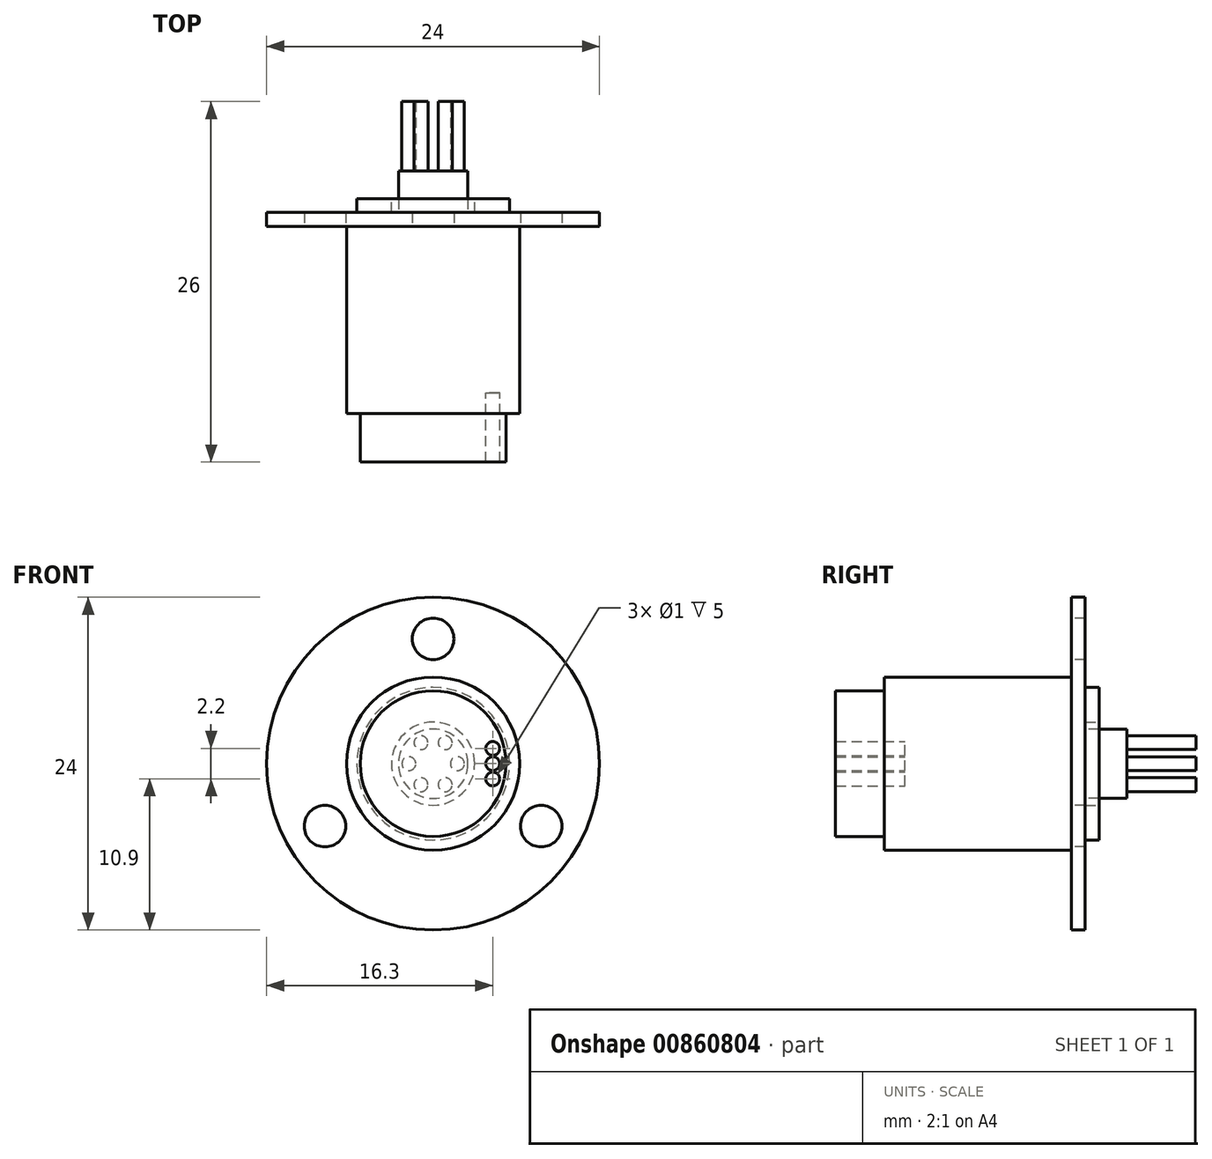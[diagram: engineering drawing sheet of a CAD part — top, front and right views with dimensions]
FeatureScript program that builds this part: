
annotation { "Feature Type Name" : "Feature", "Feature Type Description" : "" }
export const myFeature = defineFeature(function(context is Context, id is Id, definition is map)
    precondition{}
    {
        {
            var Q0;
            Q0=qCreatedBy(makeId("Front.planeOp"),FACE);
            var sketch = newSketch(context, id + "F0", { "sketchPlane" : qUnion([Q0])});
            skCircle(sketch, "E0", {"center": v(0, 0) * mm, "radius": 6.25 * mm});
            skSolve(sketch);
        }
        {
            var Q0;
            Q0=makeQuery(id+"F0.imprint","IMPRINT",FACE,{"disambiguationData":[TD([[makeQuery(id+"F0.imprint","IMPRINT",EDGE,{"derivedFrom":sQuery(id+"F0.wireOp",EDGE,"E0")}),1.0]])]});
            extrude(context, id + "F1", {"entities" : qUnion([Q0]), "depth" : 13.5 * mm, "offsetDistance" : 25 * mm});
        }
        {
            var Q0;
            Q0=makeQuery(id+"F1.opExtrude","CAP_FACE",FACE,{"disambiguationData":[OSD([sQuery(id+"F0.wireOp",EDGE,"E0")])],"isStart":true});
            var sketch = newSketch(context, id + "F2", { "sketchPlane" : qUnion([Q0])});
            skCircle(sketch, "E1", {"center": v(0, 0) * mm, "radius": 12 * mm});
            skCircle(sketch, "E2", {"center": v(0, 9) * mm, "radius": 1.5 * mm});
            skCircle(sketch, "E3.1.0", {"center": v(-7.8, -4.5) * mm, "radius": 1.5 * mm});
            skCircle(sketch, "E3.2.0", {"center": v(7.8, -4.5) * mm, "radius": 1.5 * mm});
            skSolve(sketch);
        }
        {
            var Q0;
            Q0=makeQuery(id+"F2.imprint","IMPRINT",FACE,{"disambiguationData":[TD([[makeQuery(id+"F2.imprint","IMPRINT",EDGE,{"derivedFrom":sQuery(id+"F2.wireOp",EDGE,"E1")}),1.0]])]});
            var Q1;
            Q1=makeQuery(id+"F2.imprint","IMPRINT",FACE,{"disambiguationData":[TD([[makeQuery(id+"F2.imprint","IMPRINT",EDGE,{"derivedFrom":makeQuery(id+"F1.opExtrude","CAP_EDGE",EDGE,{"disambiguationData":[OSD([sQuery(id+"F0.wireOp",EDGE,"E0")])],"isStart":true})}),-1.0]])]});
            extrude(context, id + "F3", {"entities" : qUnion([Q0, Q1]), "operationType" : NewBodyOperationType.ADD, "depth" : 1 * mm, "offsetDistance" : 25 * mm});
        }
        {
            var Q0;
            Q0=makeQuery(id+"F3.opExtrude","CAP_FACE",FACE,{"disambiguationData":[OSD([sQuery(id+"F2.wireOp",EDGE,"E1"),sQuery(id+"F2.wireOp",EDGE,"E2"),sQuery(id+"F2.wireOp",EDGE,"E3.1.0"),sQuery(id+"F2.wireOp",EDGE,"E3.2.0")])],"isStart":false});
            var sketch = newSketch(context, id + "F4", { "sketchPlane" : qUnion([Q0])});
            skCircle(sketch, "E4", {"center": v(0, 0) * mm, "radius": 2.5 * mm});
            skCircle(sketch, "E5", {"center": v(0, 0) * mm, "radius": 5.5 * mm});
            skSolve(sketch);
        }
        {
            var Q0;
            Q0=makeQuery(id+"F4.imprint","IMPRINT",FACE,{"disambiguationData":[TD([[makeQuery(id+"F4.imprint","IMPRINT",EDGE,{"derivedFrom":sQuery(id+"F4.wireOp",EDGE,"E4")}),-1.0]])]});
            extrude(context, id + "F5", {"entities" : qUnion([Q0]), "operationType" : NewBodyOperationType.ADD, "depth" : 1 * mm, "offsetDistance" : 25 * mm});
        }
        {
            var Q0;
            Q0=makeQuery(id+"F5.boolean.opBoolean","SPLIT",FACE,{"disambiguationData":[TD([makeQuery(id+"F5.opExtrude","SWEPT_FACE",FACE,{"disambiguationData":[OSD([sQuery(id+"F4.wireOp",EDGE,"E4")])]})])],"derivedFrom":makeQuery(id+"F3.opExtrude","CAP_FACE",FACE,{"disambiguationData":[OSD([sQuery(id+"F2.wireOp",EDGE,"E1"),sQuery(id+"F2.wireOp",EDGE,"E2"),sQuery(id+"F2.wireOp",EDGE,"E3.1.0"),sQuery(id+"F2.wireOp",EDGE,"E3.2.0")])],"isStart":false})});
            extrude(context, id + "F6", {"entities" : qUnion([Q0]), "operationType" : NewBodyOperationType.ADD, "depth" : 3 * mm, "offsetDistance" : 25 * mm});
        }
        {
            var Q0;
            Q0=makeQuery(id+"F5.opExtrude","CAP_FACE",FACE,{"disambiguationData":[OSD([sQuery(id+"F4.wireOp",EDGE,"E4"),sQuery(id+"F4.wireOp",EDGE,"E5")])],"isStart":false});
            var sketch = newSketch(context, id + "F7", { "sketchPlane" : qUnion([Q0])});
            skCircle(sketch, "E6", {"center": v(0, 0) * mm, "radius": 3 * mm});
            skSolve(sketch);
        }
        {
            var Q0;
            Q0=makeQuery(id+"F7.imprint","IMPRINT",FACE,{"disambiguationData":[TD([[makeQuery(id+"F7.imprint","IMPRINT",EDGE,{"derivedFrom":sQuery(id+"F7.wireOp",EDGE,"E6")}),1.0]])]});
            extrude(context, id + "F8", {"entities" : qUnion([Q0]), "operationType" : NewBodyOperationType.REMOVE, "oppositeDirection" : true, "depth" : 1 * mm, "offsetDistance" : 25 * mm});
        }
        {
            var Q0;
            Q0=makeQuery(id+"F1.opExtrude","CAP_FACE",FACE,{"disambiguationData":[OSD([sQuery(id+"F0.wireOp",EDGE,"E0")])],"isStart":false});
            var sketch = newSketch(context, id + "F9", { "sketchPlane" : qUnion([Q0])});
            skCircle(sketch, "E7", {"center": v(0, 0) * mm, "radius": 5.25 * mm});
            skSolve(sketch);
        }
        {
            var Q0;
            Q0=makeQuery(id+"F9.imprint","IMPRINT",FACE,{"disambiguationData":[TD([[makeQuery(id+"F9.imprint","IMPRINT",EDGE,{"derivedFrom":sQuery(id+"F9.wireOp",EDGE,"E7")}),1.0]])]});
            extrude(context, id + "F10", {"entities" : qUnion([Q0]), "operationType" : NewBodyOperationType.REMOVE, "oppositeDirection" : true, "depth" : 1.5 * mm, "offsetDistance" : 25 * mm});
        }
        {
            var Q0;
            Q0=makeQuery(id+"F10.boolean.opBoolean","COPY",FACE,{"derivedFrom":makeQuery(id+"F10.opExtrude","CAP_FACE",FACE,{"disambiguationData":[OSD([sQuery(id+"F9.wireOp",EDGE,"E7")])],"isStart":false})});
            var sketch = newSketch(context, id + "F11", { "sketchPlane" : qUnion([Q0])});
            skCircle(sketch, "E8", {"center": v(-4.3, 0) * mm, "radius": 0.5 * mm});
            skCircle(sketch, "E9", {"center": v(-4.3, -1.1) * mm, "radius": 0.5 * mm});
            skCircle(sketch, "E10", {"center": v(-4.3, 1.1) * mm, "radius": 0.5 * mm});
            skCircle(sketch, "E11.MirrorC", {"center": v(4.3, 1.1) * mm, "radius": 0.5 * mm});
            skCircle(sketch, "E12.MirrorC", {"center": v(4.3, 0) * mm, "radius": 0.5 * mm});
            skCircle(sketch, "E13.MirrorC", {"center": v(4.3, -1.1) * mm, "radius": 0.5 * mm});
            skSolve(sketch);
        }
        {
            var Q0;
            Q0=makeQuery(id+"F11.imprint","IMPRINT",FACE,{"disambiguationData":[TD([[makeQuery(id+"F11.imprint","IMPRINT",EDGE,{"derivedFrom":sQuery(id+"F11.wireOp",EDGE,"E9")}),1.0]])]});
            var Q1;
            Q1=makeQuery(id+"F11.imprint","IMPRINT",FACE,{"disambiguationData":[TD([[makeQuery(id+"F11.imprint","IMPRINT",EDGE,{"derivedFrom":sQuery(id+"F11.wireOp",EDGE,"E8")}),1.0]])]});
            var Q2;
            Q2=makeQuery(id+"F11.imprint","IMPRINT",FACE,{"disambiguationData":[TD([[makeQuery(id+"F11.imprint","IMPRINT",EDGE,{"derivedFrom":sQuery(id+"F11.wireOp",EDGE,"E10")}),1.0]])]});
            var Q3;
            Q3=makeQuery(id+"F11.imprint","IMPRINT",FACE,{"disambiguationData":[TD([[makeQuery(id+"F11.imprint","IMPRINT",EDGE,{"derivedFrom":sQuery(id+"F11.wireOp",EDGE,"E11.MirrorC")}),-1.0]])]});
            var Q4;
            Q4=makeQuery(id+"F11.imprint","IMPRINT",FACE,{"disambiguationData":[TD([[makeQuery(id+"F11.imprint","IMPRINT",EDGE,{"derivedFrom":sQuery(id+"F11.wireOp",EDGE,"E12.MirrorC")}),-1.0]])]});
            var Q5;
            Q5=makeQuery(id+"F11.imprint","IMPRINT",FACE,{"disambiguationData":[TD([[makeQuery(id+"F11.imprint","IMPRINT",EDGE,{"derivedFrom":sQuery(id+"F11.wireOp",EDGE,"E13.MirrorC")}),-1.0]])]});
            extrude(context, id + "F12", {"entities" : qUnion([Q0, Q1, Q2, Q3, Q4, Q5]), "operationType" : NewBodyOperationType.ADD, "depth" : 5 * mm, "offsetDistance" : 25 * mm});
        }
        {
            var Q0;
            Q0=makeQuery(id+"F6.opExtrude","CAP_FACE",FACE,{"disambiguationData":[OSD([sQuery(id+"F2.wireOp",EDGE,"E1"),sQuery(id+"F2.wireOp",EDGE,"E2"),sQuery(id+"F2.wireOp",EDGE,"E3.1.0"),sQuery(id+"F2.wireOp",EDGE,"E3.2.0")])],"isStart":false});
            var sketch = newSketch(context, id + "F13", { "sketchPlane" : qUnion([Q0])});
            skCircle(sketch, "E14", {"center": v(0, 0) * mm, "radius": 1.75 * mm, "construction": true});
            skCircle(sketch, "E15", {"center": v(-1.75, 0) * mm, "radius": 0.5 * mm});
            skCircle(sketch, "E16.1.0", {"center": v(-0.88, -1.52) * mm, "radius": 0.5 * mm});
            skCircle(sketch, "E16.2.0", {"center": v(0.87, -1.52) * mm, "radius": 0.5 * mm});
            skCircle(sketch, "E16.3.0", {"center": v(1.75, 0) * mm, "radius": 0.5 * mm});
            skCircle(sketch, "E16.4.0", {"center": v(0.88, 1.52) * mm, "radius": 0.5 * mm});
            skCircle(sketch, "E16.5.0", {"center": v(-0.88, 1.52) * mm, "radius": 0.5 * mm});
            skSolve(sketch);
        }
        {
            var Q0;
            Q0=makeQuery(id+"F13.imprint","IMPRINT",FACE,{"disambiguationData":[TD([[makeQuery(id+"F13.imprint","IMPRINT",EDGE,{"derivedFrom":sQuery(id+"F13.wireOp",EDGE,"E16.1.0")}),1.0]])]});
            var Q1;
            Q1=makeQuery(id+"F13.imprint","IMPRINT",FACE,{"disambiguationData":[TD([[makeQuery(id+"F13.imprint","IMPRINT",EDGE,{"derivedFrom":sQuery(id+"F13.wireOp",EDGE,"E16.2.0")}),1.0]])]});
            var Q2;
            Q2=makeQuery(id+"F13.imprint","IMPRINT",FACE,{"disambiguationData":[TD([[makeQuery(id+"F13.imprint","IMPRINT",EDGE,{"derivedFrom":sQuery(id+"F13.wireOp",EDGE,"E16.3.0")}),1.0]])]});
            var Q3;
            Q3=makeQuery(id+"F13.imprint","IMPRINT",FACE,{"disambiguationData":[TD([[makeQuery(id+"F13.imprint","IMPRINT",EDGE,{"derivedFrom":sQuery(id+"F13.wireOp",EDGE,"E16.4.0")}),1.0]])]});
            var Q4;
            Q4=makeQuery(id+"F13.imprint","IMPRINT",FACE,{"disambiguationData":[TD([[makeQuery(id+"F13.imprint","IMPRINT",EDGE,{"derivedFrom":sQuery(id+"F13.wireOp",EDGE,"E16.5.0")}),1.0]])]});
            var Q5;
            Q5=makeQuery(id+"F13.imprint","IMPRINT",FACE,{"disambiguationData":[TD([[makeQuery(id+"F13.imprint","IMPRINT",EDGE,{"derivedFrom":sQuery(id+"F13.wireOp",EDGE,"E15")}),1.0]])]});
            extrude(context, id + "F14", {"entities" : qUnion([Q0, Q1, Q2, Q3, Q4, Q5]), "operationType" : NewBodyOperationType.ADD, "depth" : 5 * mm, "offsetDistance" : 25 * mm});
        }
    });
